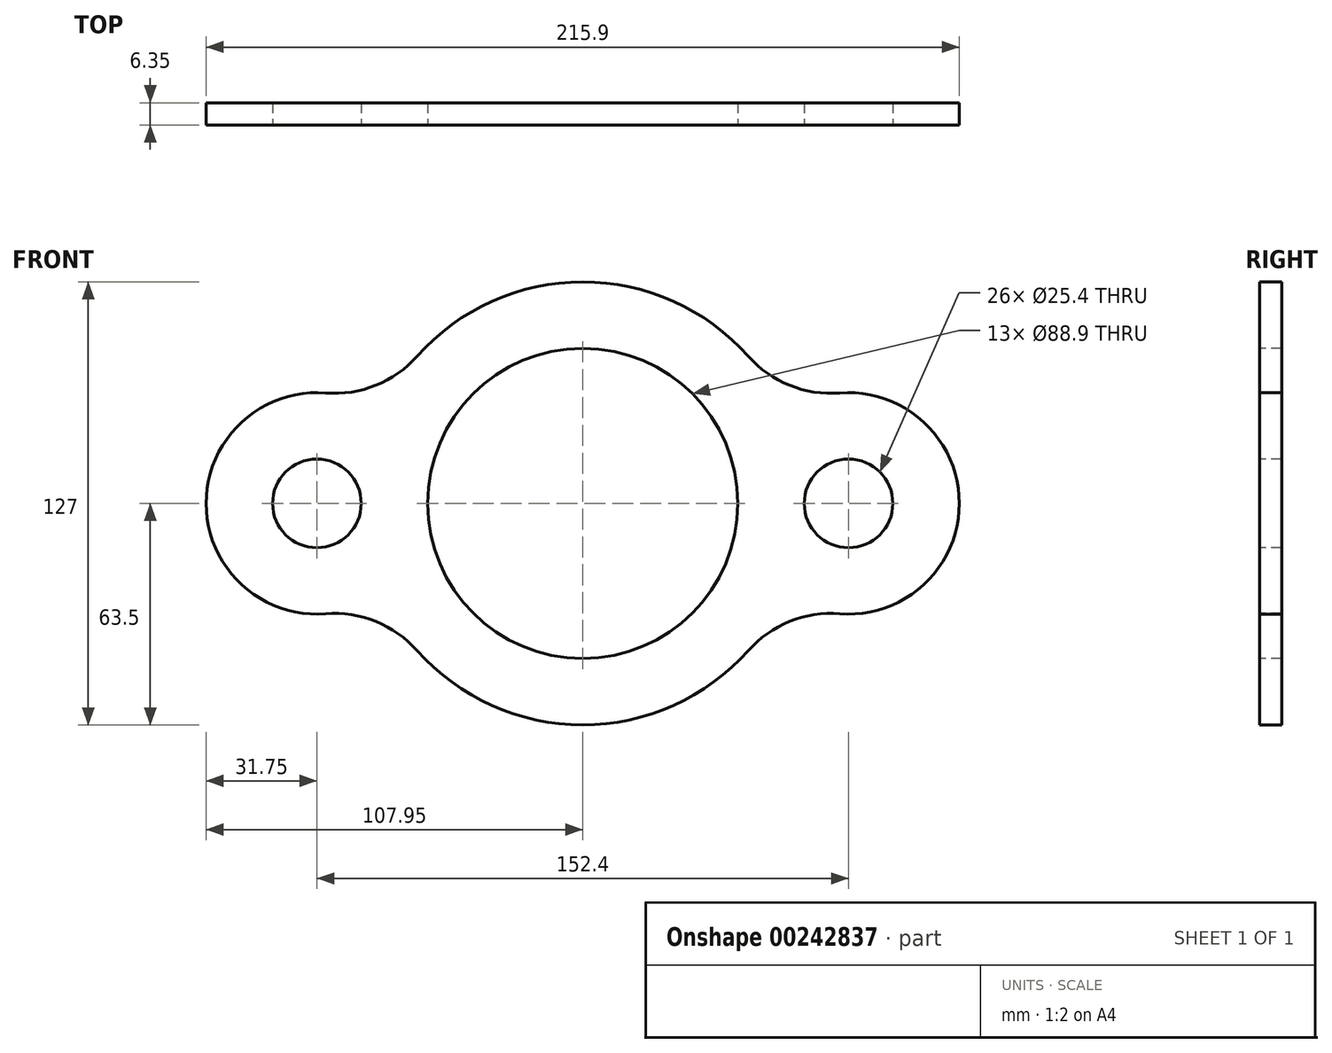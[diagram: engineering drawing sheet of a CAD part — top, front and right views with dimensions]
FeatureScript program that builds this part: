
annotation { "Feature Type Name" : "Feature", "Feature Type Description" : "" }
export const myFeature = defineFeature(function(context is Context, id is Id, definition is map)
    precondition{}
    {
        {
            var Q0;
            Q0=qCreatedBy(makeId("Front.planeOp"),FACE);
            var sketch = newSketch(context, id + "F0", { "sketchPlane" : qUnion([Q0])});
            skArc(sketch, "E0", {"start": v(-47.45, -42.2) * mm, "mid": v(0, -63.5) * mm, "end": v(47.45, -42.2) * mm});
            skCircle(sketch, "E1", {"center": v(0, 0) * mm, "radius": 44.45 * mm});
            skArc(sketch, "E2", {"start": v(-73.69, 31.65) * mm, "mid": v(-107.95, 0) * mm, "end": v(-73.69, -31.65) * mm});
            skCircle(sketch, "E3", {"center": v(-76.2, 0) * mm, "radius": 12.7 * mm});
            skArc(sketch, "E4", {"start": v(73.69, -31.65) * mm, "mid": v(107.95, 0) * mm, "end": v(73.69, 31.65) * mm});
            skCircle(sketch, "E5", {"center": v(76.2, 0) * mm, "radius": 12.7 * mm});
            skArc(sketch, "E6.trimOffspring", {"start": v(47.45, 42.2) * mm, "mid": v(0, 63.5) * mm, "end": v(-47.45, 42.2) * mm});
            skPoint(sketch, "E7.visualSharp", {"position": v(-57.94, 25.98) * mm});
            skArc(sketch, "E7.filletArc", {"start": v(-73.69, 31.65) * mm, "mid": v(-59.33, 33.84) * mm, "end": v(-47.45, 42.2) * mm});
            skPoint(sketch, "E8.visualSharp", {"position": v(-57.94, -25.98) * mm});
            skArc(sketch, "E8.filletArc", {"start": v(-47.45, -42.2) * mm, "mid": v(-59.33, -33.84) * mm, "end": v(-73.69, -31.65) * mm});
            skPoint(sketch, "E9.visualSharp", {"position": v(57.94, -25.98) * mm});
            skArc(sketch, "E9.filletArc", {"start": v(73.69, -31.65) * mm, "mid": v(59.33, -33.84) * mm, "end": v(47.45, -42.2) * mm});
            skPoint(sketch, "E10.visualSharp", {"position": v(57.94, 25.98) * mm});
            skArc(sketch, "E10.filletArc", {"start": v(47.45, 42.2) * mm, "mid": v(59.33, 33.84) * mm, "end": v(73.69, 31.65) * mm});
            skLineSegment(sketch, "E11", {"start": v(-76.2, 0) * mm, "end": v(76.2, 0) * mm, "construction": true});
            skLineSegment(sketch, "E12", {"start": v(-76.2, 0) * mm, "end": v(0, 0) * mm, "construction": true});
            skSolve(sketch);
        }
        {
            var Q0;
            Q0=makeQuery(id+"F0.imprint","IMPRINT",FACE,{"disambiguationData":[TD([[makeQuery(id+"F0.imprint","IMPRINT",EDGE,{"derivedFrom":sQuery(id+"F0.wireOp",EDGE,"E0")}),1.0]])]});
            extrude(context, id + "F1", {"entities" : qUnion([Q0]), "oppositeDirection" : true, "depth" : 6.35 * mm});
        }
    });
